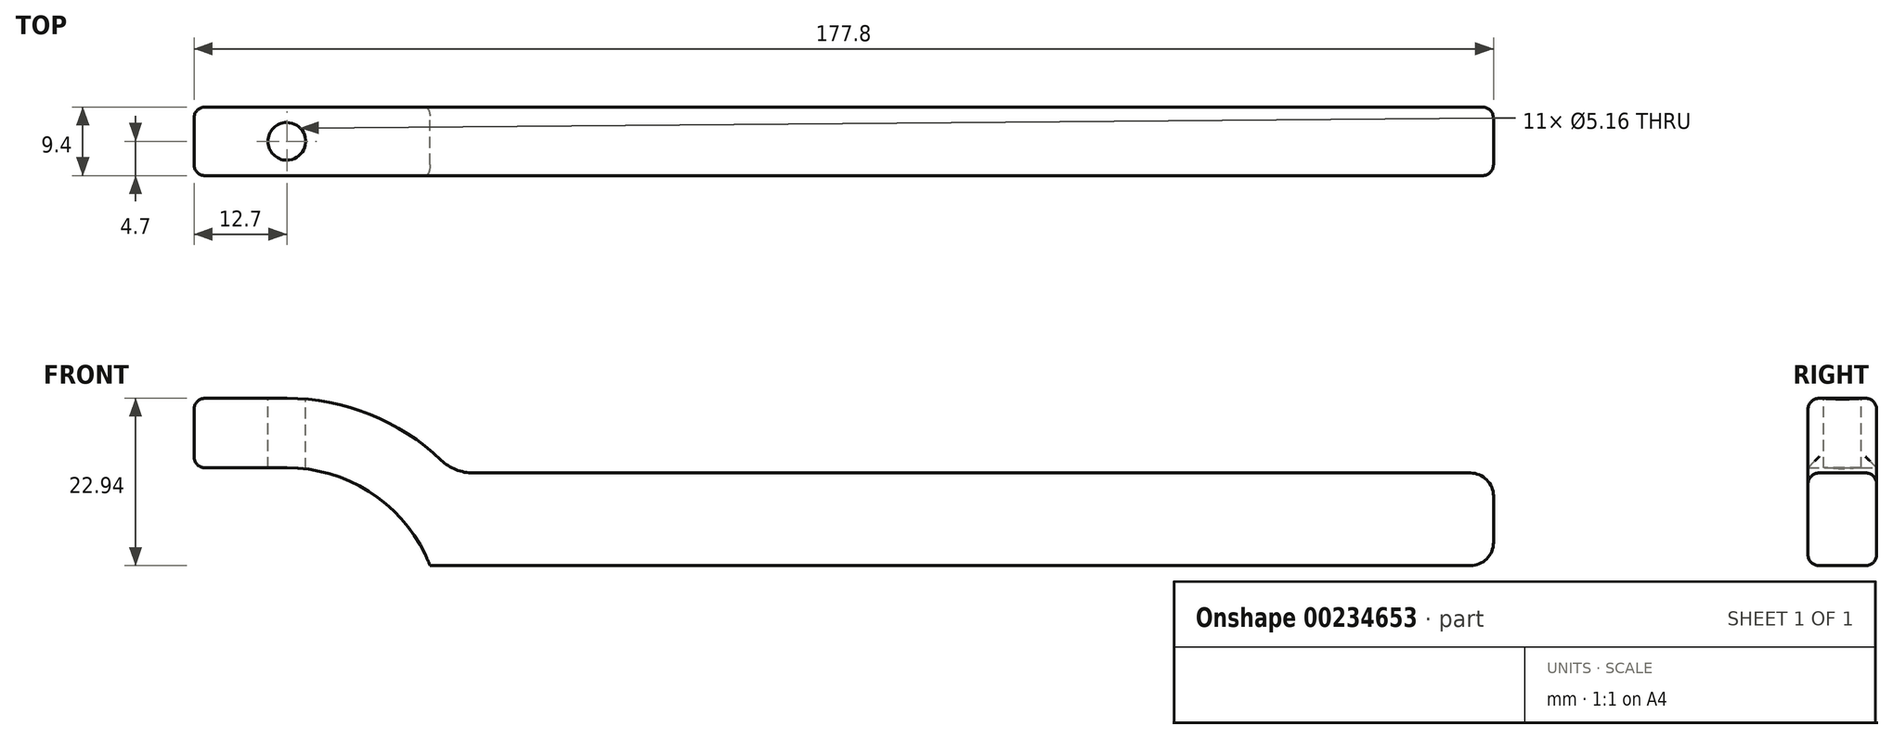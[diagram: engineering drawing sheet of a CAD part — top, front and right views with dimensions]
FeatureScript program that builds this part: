
annotation { "Feature Type Name" : "Feature", "Feature Type Description" : "" }
export const myFeature = defineFeature(function(context is Context, id is Id, definition is map)
    precondition{}
    {
        {
            var Q0;
            Q0=qCreatedBy(makeId("Front.planeOp"),FACE);
            var sketch = newSketch(context, id + "F0", { "sketchPlane" : qUnion([Q0])});
            skLineSegment(sketch, "E0", {"start": v(19.6, 7.62) * mm, "end": v(165.1, 7.62) * mm});
            skLineSegment(sketch, "E1", {"start": v(165.1, 7.62) * mm, "end": v(165.1, 20.32) * mm});
            skLineSegment(sketch, "E2", {"start": v(165.1, 20.32) * mm, "end": v(22.82, 20.32) * mm});
            skArc(sketch, "E3", {"start": v(0, 30.56) * mm, "mid": v(12.5, 27.88) * mm, "end": v(22.82, 20.32) * mm});
            skLineSegment(sketch, "E4", {"start": v(0, 30.56) * mm, "end": v(-12.7, 30.56) * mm});
            skLineSegment(sketch, "E5", {"start": v(-12.7, 30.56) * mm, "end": v(-12.7, 21.03) * mm});
            skLineSegment(sketch, "E6", {"start": v(-12.7, 21.03) * mm, "end": v(0, 21.03) * mm});
            skArc(sketch, "E7", {"start": v(19.6, 7.62) * mm, "mid": v(11.88, 17.36) * mm, "end": v(0, 21.03) * mm});
            skSolve(sketch);
        }
        {
            var Q0;
            Q0 = qSketchRegion(id + "F0", true);
            extrude(context, id + "F1", {"entities" : qUnion([Q0]), "depth" : 9.4 * mm, "symmetric" : true});
        }
        {
            var Q0;
            Q0=makeQuery(id+"F1.opExtrude","SWEPT_EDGE",EDGE,{"disambiguationData":[OSD([sQuery(id+"F0.wireOp",EDGE,"E1"),sQuery(id+"F0.wireOp",EDGE,"E2")])]});
            var Q1;
            Q1=makeQuery(id+"F1.opExtrude","SWEPT_EDGE",EDGE,{"disambiguationData":[OSD([sQuery(id+"F0.wireOp",EDGE,"E0"),sQuery(id+"F0.wireOp",EDGE,"E1")])]});
            fillet(context, id + "F2", {"entities" : qUnion([Q0, Q1]), "radius" : 3.17 * mm, "tangentPropagation" : true, "allowEdgeOverflow" : false});
        }
        {
            var Q0;
            Q0=makeQuery(id+"F1.opExtrude","SWEPT_FACE",FACE,{"disambiguationData":[OSD([sQuery(id+"F0.wireOp",EDGE,"E5")])]});
            fillet(context, id + "F3", {"entities" : qUnion([Q0]), "radius" : 1.52 * mm, "tangentPropagation" : true, "allowEdgeOverflow" : false});
        }
        {
            var Q0;
            Q0=makeQuery(id+"F1.opExtrude","SWEPT_EDGE",EDGE,{"disambiguationData":[OSD([sQuery(id+"F0.wireOp",EDGE,"E2"),sQuery(id+"F0.wireOp",EDGE,"E3")])]});
            fillet(context, id + "F4", {"entities" : qUnion([Q0]), "radius" : 6.35 * mm, "tangentPropagation" : true, "allowEdgeOverflow" : false});
        }
        {
            var Q0;
            Q0=makeQuery(id+"F1.opExtrude","CAP_EDGE",EDGE,{"disambiguationData":[OSD([sQuery(id+"F0.wireOp",EDGE,"E4")])],"isStart":false});
            var Q1;
            Q1=makeQuery(id+"F1.opExtrude","CAP_EDGE",EDGE,{"disambiguationData":[OSD([sQuery(id+"F0.wireOp",EDGE,"E4")])],"isStart":true});
            fillet(context, id + "F5", {"entities" : qUnion([Q0, Q1]), "radius" : 1.52 * mm, "tangentPropagation" : true, "allowEdgeOverflow" : false});
        }
        {
            var Q0;
            Q0=makeQuery(id+"F1.opExtrude","SWEPT_FACE",FACE,{"disambiguationData":[OSD([sQuery(id+"F0.wireOp",EDGE,"E4")])]});
            var sketch = newSketch(context, id + "F6", { "sketchPlane" : qUnion([Q0])});
            skCircle(sketch, "E8", {"center": v(0, 0) * mm, "radius": 2.58 * mm});
            skSolve(sketch);
        }
        {
            var Q0;
            Q0 = qSketchRegion(id + "F6", true);
            extrude(context, id + "F7", {"entities" : qUnion([Q0]), "operationType" : NewBodyOperationType.REMOVE, "endBound" : BoundingType.THROUGH_ALL, "oppositeDirection" : true, "depth" : 25.4 * mm});
        }
    });
